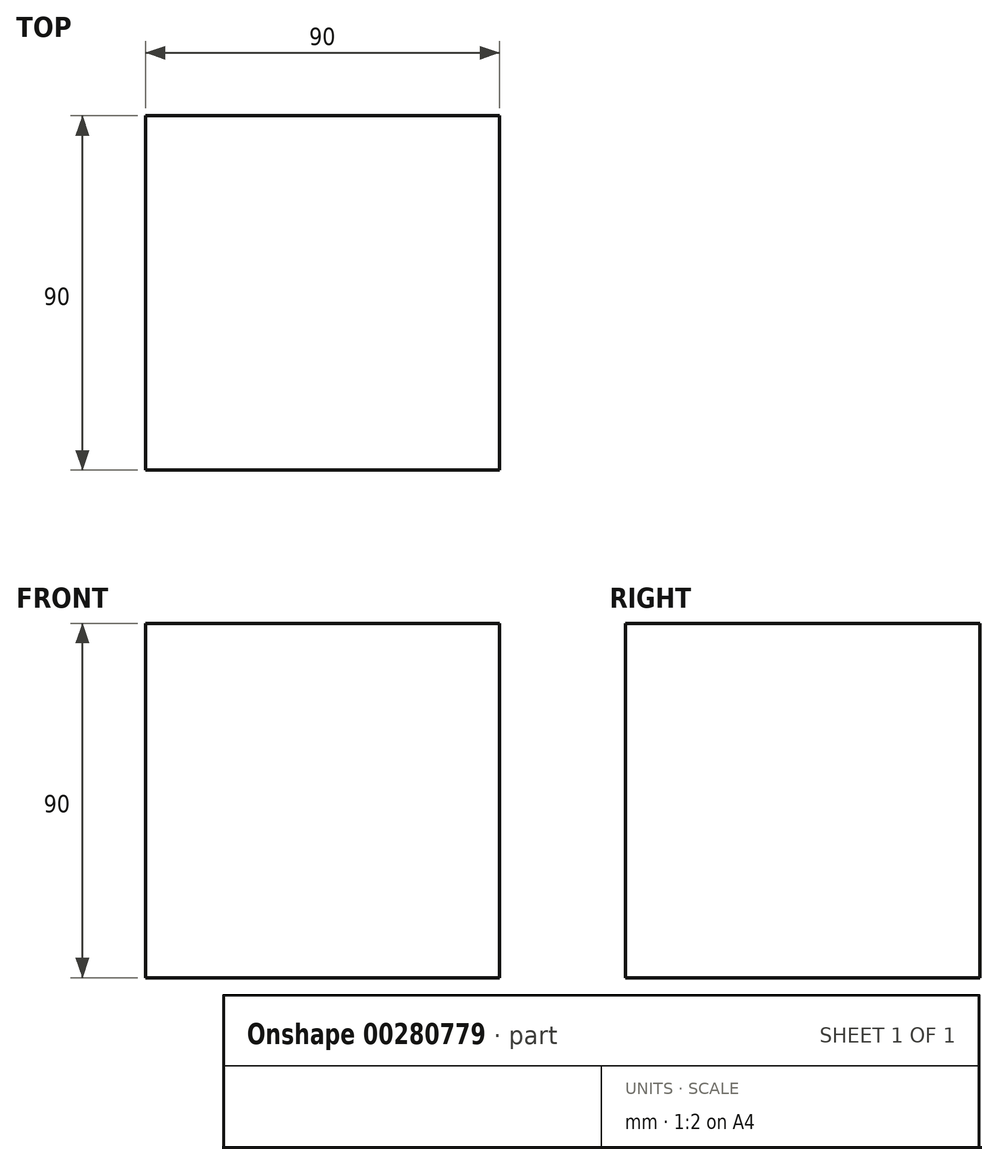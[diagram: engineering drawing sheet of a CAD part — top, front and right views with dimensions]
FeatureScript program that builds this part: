
annotation { "Feature Type Name" : "Feature", "Feature Type Description" : "" }
export const myFeature = defineFeature(function(context is Context, id is Id, definition is map)
    precondition{}
    {
        {
            var Q0;
            Q0=qCreatedBy(makeId("Front.planeOp"),FACE);
            var sketch = newSketch(context, id + "F0", { "sketchPlane" : qUnion([Q0])});
            skLineSegment(sketch, "E0.bottom", {"start": v(45, 45) * mm, "end": v(-45, 45) * mm});
            skLineSegment(sketch, "E0.top", {"start": v(45, -45) * mm, "end": v(-45, -45) * mm});
            skLineSegment(sketch, "E0.left", {"start": v(45, 45) * mm, "end": v(45, -45) * mm});
            skLineSegment(sketch, "E0.right", {"start": v(-45, 45) * mm, "end": v(-45, -45) * mm});
            skPoint(sketch, "E0.middle", {"position": v(0, 0) * mm});
            skSolve(sketch);
        }
        {
            var Q0;
            Q0=makeQuery(id+"F0.imprint","IMPRINT",FACE,{"disambiguationData":[TD([[makeQuery(id+"F0.imprint","IMPRINT",EDGE,{"derivedFrom":sQuery(id+"F0.wireOp",EDGE,"E0.bottom")}),1.0]])]});
            extrude(context, id + "F1", {"entities" : qUnion([Q0]), "depth" : 90 * mm});
        }
    });
